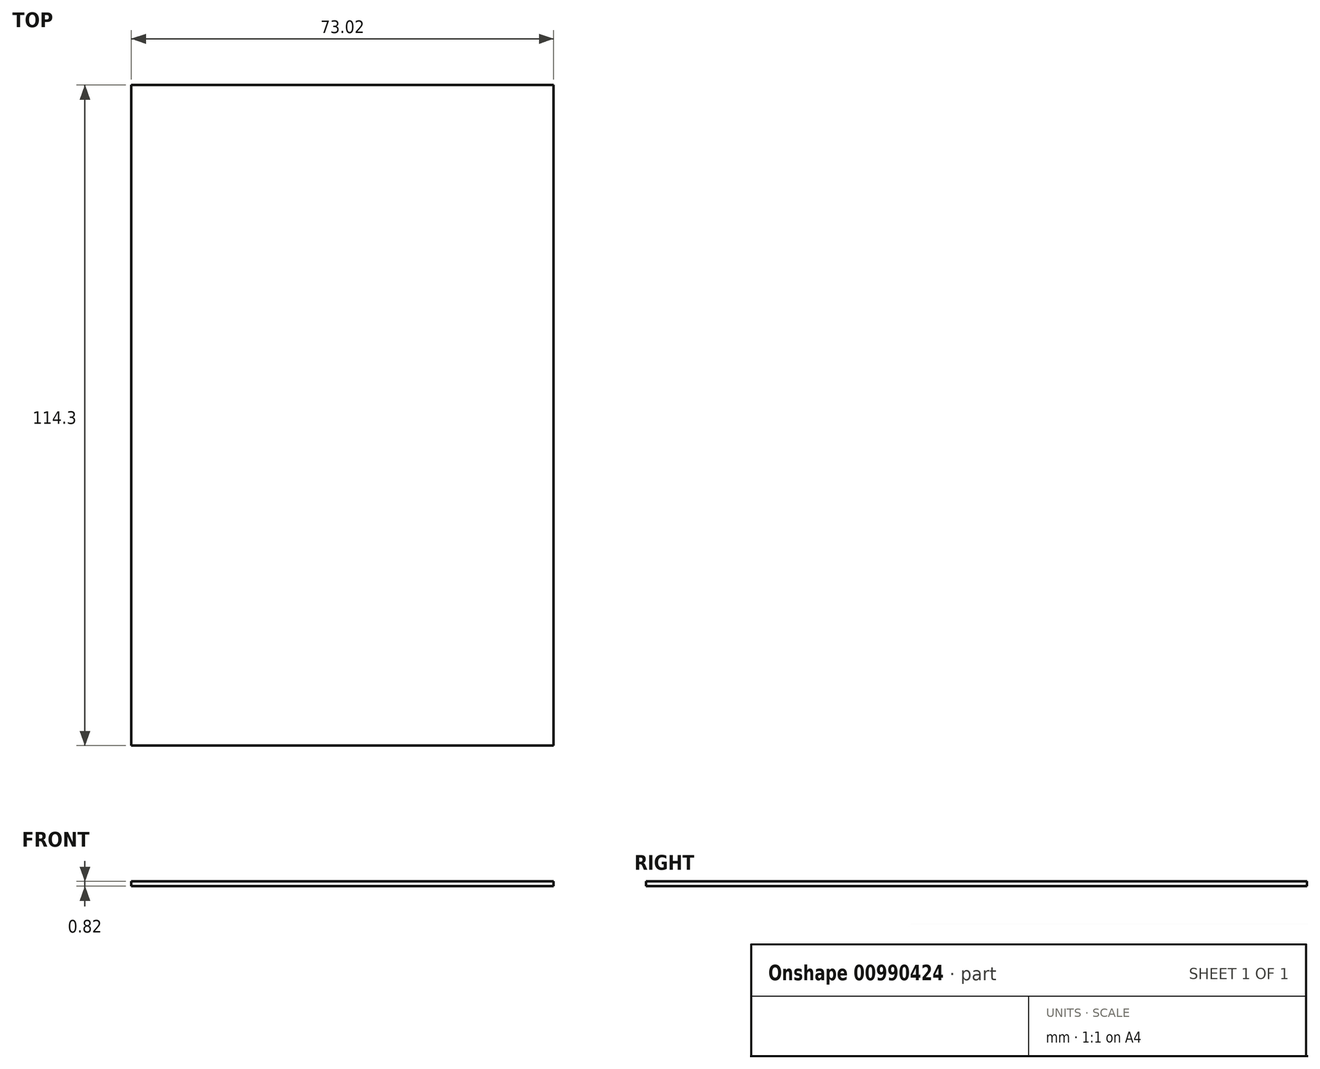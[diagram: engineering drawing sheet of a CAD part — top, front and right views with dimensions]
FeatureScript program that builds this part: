
annotation { "Feature Type Name" : "Feature", "Feature Type Description" : "" }
export const myFeature = defineFeature(function(context is Context, id is Id, definition is map)
    precondition{}
    {
        {
            var Q0;
            Q0=qCreatedBy(makeId("Top.planeOp"),FACE);
            var sketch = newSketch(context, id + "F0", { "sketchPlane" : qUnion([Q0])});
            skLineSegment(sketch, "E0.bottom", {"start": v(-36.51, 57.15) * mm, "end": v(36.51, 57.15) * mm});
            skLineSegment(sketch, "E0.top", {"start": v(-36.51, -57.15) * mm, "end": v(36.51, -57.15) * mm});
            skLineSegment(sketch, "E0.left", {"start": v(-36.51, 57.15) * mm, "end": v(-36.51, -57.15) * mm});
            skLineSegment(sketch, "E0.right", {"start": v(36.51, 57.15) * mm, "end": v(36.51, -57.15) * mm});
            skPoint(sketch, "E0.middle", {"position": v(0, 0) * mm});
            skSolve(sketch);
        }
        {
            var Q0;
            Q0=makeQuery(id+"F0.imprint","IMPRINT",FACE,{"disambiguationData":[TD([[makeQuery(id+"F0.imprint","IMPRINT",EDGE,{"derivedFrom":sQuery(id+"F0.wireOp",EDGE,"E0.bottom")}),-1.0]])]});
            extrude(context, id + "F1", {"entities" : qUnion([Q0]), "depth" : 0.82 * mm, "offsetDistance" : 25.4 * mm});
        }
    });
